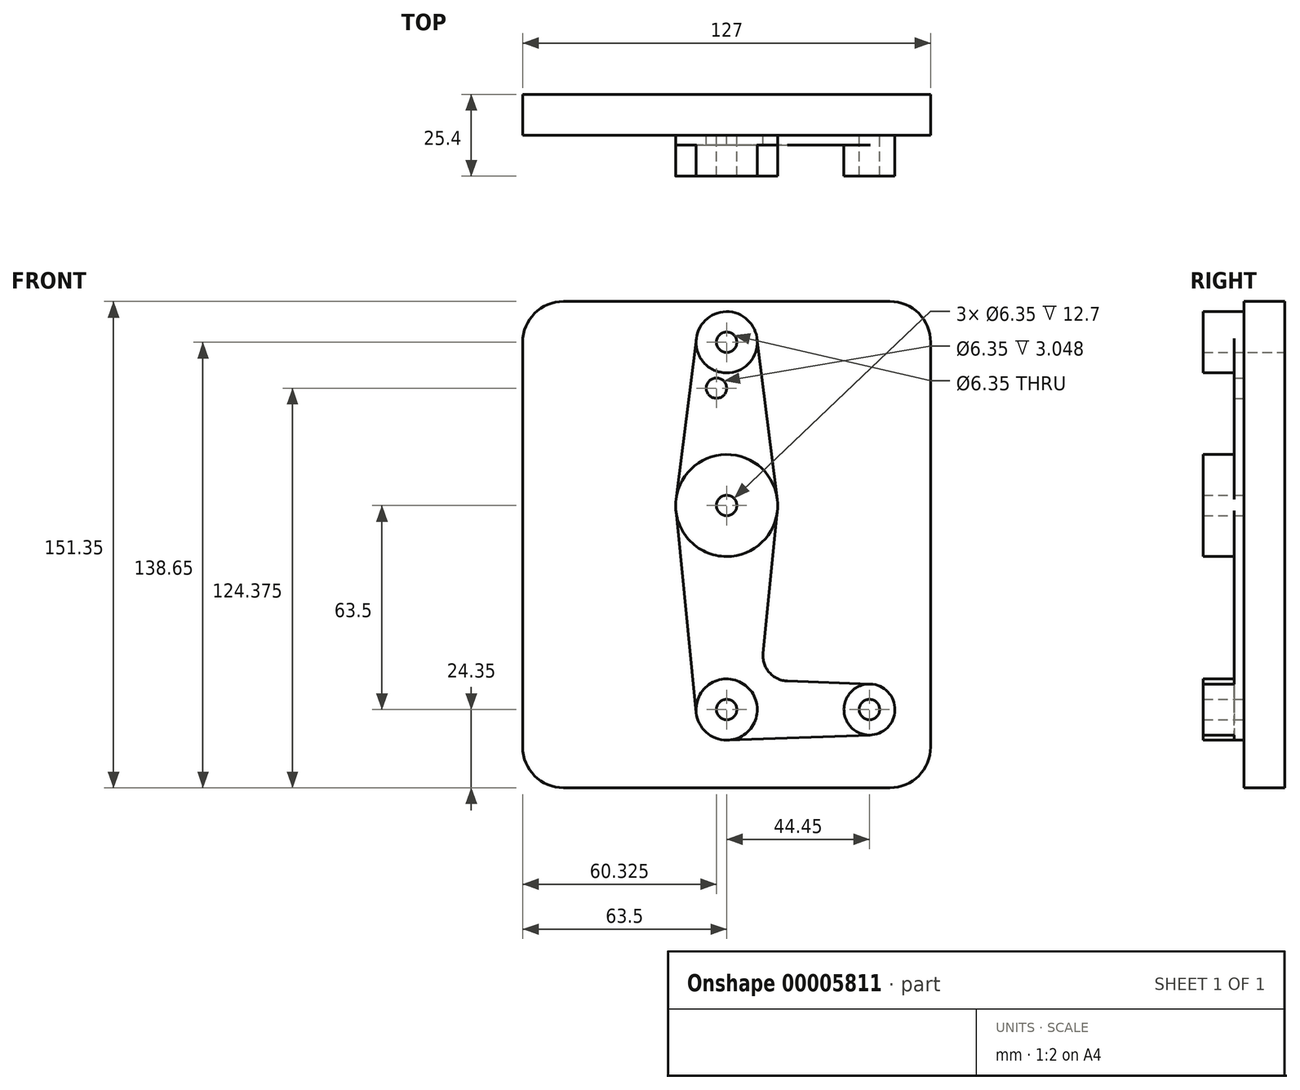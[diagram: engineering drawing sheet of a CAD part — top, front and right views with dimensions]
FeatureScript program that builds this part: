
annotation { "Feature Type Name" : "Feature", "Feature Type Description" : "" }
export const myFeature = defineFeature(function(context is Context, id is Id, definition is map)
    precondition{}
    {
        {
            var Q0;
            Q0=qCreatedBy(makeId("Front.planeOp"),FACE);
            var sketch = newSketch(context, id + "F0", { "sketchPlane" : qUnion([Q0])});
            skLineSegment(sketch, "E0", {"start": v(0, 0) * mm, "end": v(0, 114.3) * mm, "construction": true});
            skLineSegment(sketch, "E1", {"start": v(0, 0) * mm, "end": v(44.45, 0) * mm, "construction": true});
            skCircle(sketch, "E2", {"center": v(0, 114.3) * mm, "radius": 9.53 * mm});
            skCircle(sketch, "E3", {"center": v(0, 63.5) * mm, "radius": 15.88 * mm});
            skCircle(sketch, "E4", {"center": v(0, 0) * mm, "radius": 9.53 * mm});
            skCircle(sketch, "E5", {"center": v(44.45, 0) * mm, "radius": 7.94 * mm});
            skLineSegment(sketch, "E6", {"start": v(9.45, 115.5) * mm, "end": v(15.75, 65.48) * mm});
            skLineSegment(sketch, "E7", {"start": v(15.8, 61.91) * mm, "end": v(11.34, 17.6) * mm});
            skLineSegment(sketch, "E8", {"start": v(-9.48, -0.95) * mm, "end": v(-15.8, 61.91) * mm});
            skLineSegment(sketch, "E9", {"start": v(-15.75, 65.48) * mm, "end": v(-9.45, 115.5) * mm});
            skLineSegment(sketch, "E10", {"start": v(44.73, 7.93) * mm, "end": v(18.97, 8.85) * mm});
            skLineSegment(sketch, "E11", {"start": v(44.73, -7.93) * mm, "end": v(0.34, -9.52) * mm});
            skCircle(sketch, "E12", {"center": v(0, 114.3) * mm, "radius": 3.18 * mm});
            skCircle(sketch, "E13", {"center": v(0, 63.5) * mm, "radius": 3.18 * mm});
            skCircle(sketch, "E14", {"center": v(0, 0) * mm, "radius": 3.18 * mm});
            skCircle(sketch, "E15", {"center": v(44.45, 0) * mm, "radius": 3.18 * mm});
            skCircle(sketch, "E16", {"center": v(-3.18, 100.03) * mm, "radius": 3.18 * mm});
            skArc(sketch, "E17.filletArc", {"start": v(11.34, 17.6) * mm, "mid": v(13.26, 11.57) * mm, "end": v(18.97, 8.85) * mm});
            skSolve(sketch);
        }
        {
            var Q0;
            Q0 = qSketchRegion(id + "F0", true);
            extrude(context, id + "F1", {"entities" : qUnion([Q0]), "depth" : 3.05 * mm});
        }
        {
            var Q0;
            Q0=qCreatedBy(makeId("Front.planeOp"),FACE);
            var sketch = newSketch(context, id + "F2", { "sketchPlane" : qUnion([Q0])});
            skLineSegment(sketch, "E18.bottom", {"start": v(63.5, 127) * mm, "end": v(-63.5, 127) * mm});
            skLineSegment(sketch, "E18.top", {"start": v(63.5, -24.35) * mm, "end": v(-63.5, -24.35) * mm});
            skLineSegment(sketch, "E18.left", {"start": v(63.5, 127) * mm, "end": v(63.5, -24.35) * mm});
            skLineSegment(sketch, "E18.right", {"start": v(-63.5, 127) * mm, "end": v(-63.5, -24.35) * mm});
            skCircle(sketch, "E19.0", {"center": v(0, 114.3) * mm, "radius": 3.18 * mm});
            skSolve(sketch);
        }
        {
            var Q0;
            Q0 = qSketchRegion(id + "F2", true);
            extrude(context, id + "F3", {"entities" : qUnion([Q0]), "oppositeDirection" : true, "depth" : 12.7 * mm});
        }
        {
            var Q0;
            Q0=makeQuery(id+"F3.opExtrude","SWEPT_EDGE",EDGE,{"disambiguationData":[OSD([sQuery(id+"F2.wireOp",EDGE,"E18.bottom"),sQuery(id+"F2.wireOp",EDGE,"E18.left")])]});
            var Q1;
            Q1=makeQuery(id+"F3.opExtrude","SWEPT_EDGE",EDGE,{"disambiguationData":[OSD([sQuery(id+"F2.wireOp",EDGE,"E18.top"),sQuery(id+"F2.wireOp",EDGE,"E18.right")])]});
            var Q2;
            Q2=makeQuery(id+"F3.opExtrude","SWEPT_EDGE",EDGE,{"disambiguationData":[OSD([sQuery(id+"F2.wireOp",EDGE,"E18.top"),sQuery(id+"F2.wireOp",EDGE,"E18.left")])]});
            var Q3;
            Q3=makeQuery(id+"F3.opExtrude","SWEPT_EDGE",EDGE,{"disambiguationData":[OSD([sQuery(id+"F2.wireOp",EDGE,"E18.bottom"),sQuery(id+"F2.wireOp",EDGE,"E18.right")])]});
            fillet(context, id + "F4", {"entities" : qUnion([Q0, Q1, Q2, Q3]), "radius" : 12.7 * mm, "tangentPropagation" : true, "allowEdgeOverflow" : false});
        }
        {
            var Q0;
            Q0=makeQuery(id+"F0.imprint","IMPRINT",FACE,{"disambiguationData":[TD([[makeQuery(id+"F0.imprint","IMPRINT",EDGE,{"derivedFrom":sQuery(id+"F0.wireOp",EDGE,"E12")}),-1.0]])]});
            var Q1;
            Q1=makeQuery(id+"F0.imprint","IMPRINT",FACE,{"disambiguationData":[TD([[makeQuery(id+"F0.imprint","IMPRINT",EDGE,{"derivedFrom":sQuery(id+"F0.wireOp",EDGE,"E13")}),-1.0]])]});
            var Q2;
            Q2=makeQuery(id+"F0.imprint","IMPRINT",FACE,{"disambiguationData":[TD([[makeQuery(id+"F0.imprint","IMPRINT",EDGE,{"derivedFrom":sQuery(id+"F0.wireOp",EDGE,"E14")}),-1.0]])]});
            var Q3;
            Q3=makeQuery(id+"F0.imprint","IMPRINT",FACE,{"disambiguationData":[TD([[makeQuery(id+"F0.imprint","IMPRINT",EDGE,{"derivedFrom":sQuery(id+"F0.wireOp",EDGE,"E15")}),-1.0]])]});
            extrude(context, id + "F5", {"entities" : qUnion([Q0, Q1, Q2, Q3]), "operationType" : NewBodyOperationType.ADD, "depth" : 12.7 * mm});
        }
    });
